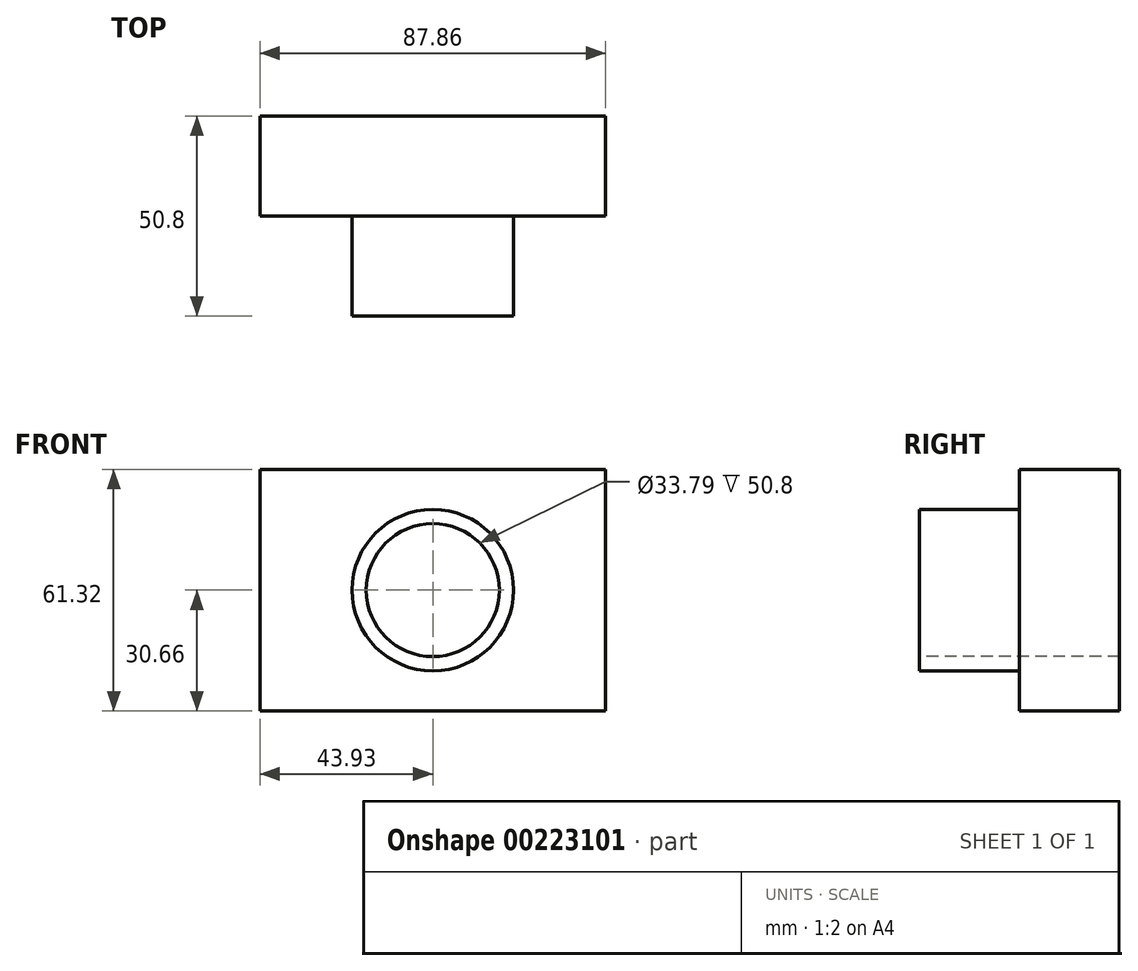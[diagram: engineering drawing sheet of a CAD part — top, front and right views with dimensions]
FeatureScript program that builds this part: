
annotation { "Feature Type Name" : "Feature", "Feature Type Description" : "" }
export const myFeature = defineFeature(function(context is Context, id is Id, definition is map)
    precondition{}
    {
        {
            var Q0;
            Q0=qCreatedBy(makeId("Front.planeOp"),FACE);
            var sketch = newSketch(context, id + "F0", { "sketchPlane" : qUnion([Q0])});
            skLineSegment(sketch, "E0.bottom", {"start": v(43.93, 30.66) * mm, "end": v(-43.93, 30.66) * mm});
            skLineSegment(sketch, "E0.top", {"start": v(43.93, -30.66) * mm, "end": v(-43.93, -30.66) * mm});
            skLineSegment(sketch, "E0.left", {"start": v(43.93, 30.66) * mm, "end": v(43.93, -30.66) * mm});
            skLineSegment(sketch, "E0.right", {"start": v(-43.93, 30.66) * mm, "end": v(-43.93, -30.66) * mm});
            skPoint(sketch, "E0.middle", {"position": v(0, 0) * mm});
            skSolve(sketch);
        }
        {
            var Q0;
            Q0 = qSketchRegion(id + "F0", true);
            extrude(context, id + "F1", {"entities" : qUnion([Q0]), "depth" : 25.4 * mm});
        }
        {
            var Q0;
            Q0=makeQuery(id+"F1.opExtrude","CAP_FACE",FACE,{"disambiguationData":[OSD([sQuery(id+"F0.wireOp",EDGE,"E0.bottom"),sQuery(id+"F0.wireOp",EDGE,"E0.top"),sQuery(id+"F0.wireOp",EDGE,"E0.left"),sQuery(id+"F0.wireOp",EDGE,"E0.right")])],"isStart":false});
            var sketch = newSketch(context, id + "F2", { "sketchPlane" : qUnion([Q0])});
            skCircle(sketch, "E1", {"center": v(0, 0) * mm, "radius": 20.51 * mm});
            skSolve(sketch);
        }
        {
            var Q0;
            Q0 = qSketchRegion(id + "F2", true);
            extrude(context, id + "F3", {"entities" : qUnion([Q0]), "operationType" : NewBodyOperationType.ADD, "depth" : 25.4 * mm});
        }
        {
            var Q0;
            Q0=qCreatedBy(makeId("Front.planeOp"),FACE);
            var sketch = newSketch(context, id + "F4", { "sketchPlane" : qUnion([Q0])});
            skCircle(sketch, "E2", {"center": v(0, 0) * mm, "radius": 15.85 * mm});
            skSolve(sketch);
        }
        {
            var Q0;
            Q0 = qSketchRegion(id + "F4", true);
            extrude(context, id + "F5", {"entities" : qUnion([Q0]), "operationType" : NewBodyOperationType.REMOVE, "oppositeDirection" : true, "depth" : 50.8 * mm});
        }
        {
            var Q0;
            Q0=makeQuery(id+"F3.opExtrude","CAP_FACE",FACE,{"disambiguationData":[OSD([sQuery(id+"F2.wireOp",EDGE,"E1")])],"isStart":false});
            var sketch = newSketch(context, id + "F6", { "sketchPlane" : qUnion([Q0])});
            skCircle(sketch, "E3", {"center": v(0, 0) * mm, "radius": 16.9 * mm});
            skSolve(sketch);
        }
        {
            var Q0;
            Q0=makeQuery(id+"F6.imprint","IMPRINT",FACE,{"disambiguationData":[TD([[makeQuery(id+"F6.imprint","IMPRINT",EDGE,{"derivedFrom":sQuery(id+"F6.wireOp",EDGE,"E3")}),1.0]])]});
            extrude(context, id + "F7", {"entities" : qUnion([Q0]), "operationType" : NewBodyOperationType.REMOVE, "oppositeDirection" : true, "depth" : 76.2 * mm});
        }
    });
